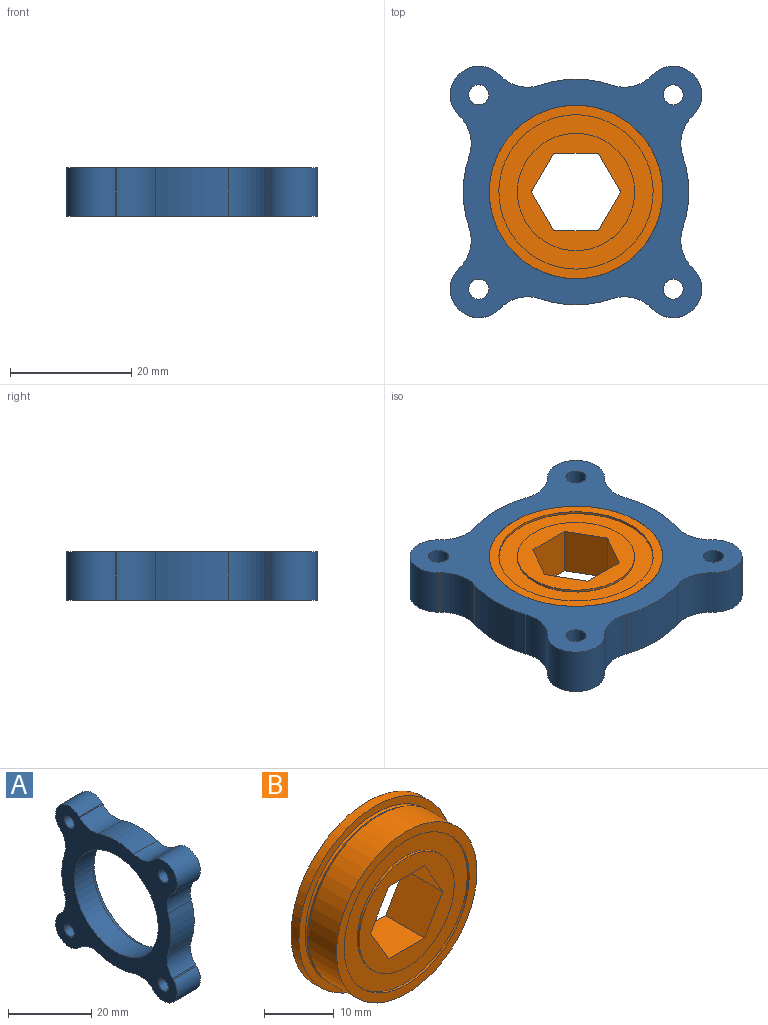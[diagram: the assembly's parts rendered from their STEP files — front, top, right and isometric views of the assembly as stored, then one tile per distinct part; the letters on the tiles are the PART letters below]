
ASSEMBLY  parts=2 mates=1
PART A: 33 faces, bbox 7.9x41.4x41.4 mm
  f0: cylinder r=4.7mm len=8.03mm, axis (1,0,0), area 117.3mm2, adj f1,f15,f17,f19
  f1: plane 7.94x0.22mm, normal (0,0.71,0.71), area 2.4mm2, adj f0,f17,f19,f25
  f2: cylinder r=18.56mm len=11.87mm, axis (1,0,0), area 95.9mm2, adj f17,f19,f25,f26
  f3: plane 7.94x0.22mm, normal (0,-0.71,0.71), area 2.4mm2, adj f4,f17,f19,f26
  f4: cylinder r=4.7mm len=8.03mm, axis (1,0,0), area 117.3mm2, adj f3,f5,f17,f19
  f5: plane 7.94x0.22mm, normal (0,0.71,-0.71), area 2.4mm2, adj f4,f17,f19,f27
  f6: cylinder r=18.56mm len=11.87mm, axis (1,0,0), area 95.9mm2, adj f17,f19,f27,f28
  f7: plane 7.94x0.22mm, normal (0,0.71,0.71), area 2.4mm2, adj f8,f17,f19,f28
  f8: cylinder r=4.7mm len=8.03mm, axis (1,0,0), area 117.3mm2, adj f7,f9,f17,f19
  f9: plane 7.94x0.22mm, normal (0,-0.71,-0.71), area 2.4mm2, adj f8,f17,f19,f29
  f10: cylinder r=18.56mm len=11.87mm, axis (1,0,0), area 95.9mm2, adj f17,f19,f29,f30
  f11: plane 7.94x0.22mm, normal (0,0.71,-0.71), area 2.4mm2, adj f12,f17,f19,f30
  f12: cylinder r=4.7mm len=8.03mm, axis (1,0,0), area 117.3mm2, adj f11,f13,f17,f19
  f13: plane 7.94x0.22mm, normal (0,-0.71,0.71), area 2.4mm2, adj f12,f17,f19,f31
  f14: cylinder r=18.56mm len=11.87mm, axis (1,0,0), area 95.9mm2, adj f17,f19,f31,f32
  f15: plane 7.94x0.22mm, normal (0,-0.71,-0.71), area 2.4mm2, adj f0,f17,f19,f32
  f16: cylinder r=15.56mm len=31.12mm, axis (1,0,0), area 155.2mm2, adj f17,f18
  f17: plane 41.41x41.41mm, normal (1,0,0), area 612.1mm2, adj f0,f1,f2,f3,f4,f5,f6,f7
  f18: plane 31.12x31.12mm, normal (1,0,0), area 120.2mm2, adj f16,f20
  f19: plane 41.41x41.41mm, normal (-1,0,0), area 732.3mm2, adj f0,f1,f2,f3,f4,f5,f6,f7
  f20: cylinder r=14.27mm len=28.55mm, axis (1,0,0), area 569.5mm2, adj f18,f19
  f21: cylinder r=1.65mm len=7.94mm, axis (-1,0,0), area 82.3mm2, adj f17,f19
  f22: cylinder r=1.65mm len=7.94mm, axis (-1,0,0), area 82.3mm2, adj f17,f19
  f23: cylinder r=1.65mm len=7.94mm, axis (-1,0,0), area 82.3mm2, adj f17,f19
  f24: cylinder r=1.65mm len=7.94mm, axis (-1,0,0), area 82.3mm2, adj f17,f19
  f25: cylinder r=6.35mm len=7.94mm, axis (1,0,0), area 56mm2, adj f1,f2,f17,f19
  f26: cylinder r=6.35mm len=7.94mm, axis (1,0,0), area 56mm2, adj f2,f3,f17,f19
  f27: cylinder r=6.35mm len=7.94mm, axis (1,0,0), area 56mm2, adj f5,f6,f17,f19
  f28: cylinder r=6.35mm len=7.94mm, axis (1,0,0), area 56mm2, adj f6,f7,f17,f19
  f29: cylinder r=6.35mm len=7.94mm, axis (1,0,0), area 56mm2, adj f9,f10,f17,f19
  f30: cylinder r=6.35mm len=7.94mm, axis (1,0,0), area 56mm2, adj f10,f11,f17,f19
  f31: cylinder r=6.35mm len=7.94mm, axis (1,0,0), area 56mm2, adj f13,f14,f17,f19
  f32: cylinder r=6.35mm len=7.94mm, axis (1,0,0), area 56mm2, adj f14,f15,f17,f19
PART B: 21 faces, bbox 31.1x7.9x31.1 mm
  f0: torus R=14.27mm, axis (0,1,0), area 46.4mm2, adj f4,f10
  f1: cylinder r=9.65mm len=19.3mm, axis (0,1,0), area 23.1mm2, adj f12,f13
  f2: cylinder r=12.7mm len=25.4mm, axis (0,1,0), area 30.4mm2, adj f11,f12
  f3: cylinder r=14.27mm len=28.55mm, axis (0,1,0), area 502.3mm2, adj f4,f11
  f4: cone r=14.06mm half-angle=30deg, axis (0,-1,0), area 38.5mm2, adj f0,f3
  f5: cylinder r=15.56mm len=31.12mm, axis (0,1,0), area 155.2mm2, adj f9,f10
  f6: cylinder r=12.7mm len=25.4mm, axis (0,1,0), area 30.4mm2, adj f8,f9
  f7: cylinder r=9.65mm len=19.3mm, axis (0,1,0), area 23.1mm2, adj f8,f14
  f8: plane 25.4x25.4mm, normal (0,1,0), area 214mm2, adj f6,f7
  f9: plane 31.12x31.12mm, normal (0,1,0), area 253.7mm2, adj f5,f6
  f10: plane 31.12x31.12mm, normal (0,-1,0), area 120.2mm2, adj f0,f5
  f11: plane 28.55x28.55mm, normal (0,-1,0), area 133.5mm2, adj f2,f3
  f12: plane 25.4x25.4mm, normal (0,-1,0), area 214mm2, adj f1,f2
  f13: plane 19.3x19.3mm, normal (0,-1,0), area 152.6mm2, adj f1,f15,f16,f17,f18,f19,f20
  f14: plane 19.3x19.3mm, normal (0,1,0), area 152.6mm2, adj f7,f15,f16,f17,f18,f19,f20
  f15: plane 7.94x6.36mm, normal (-0.87,0,0.5), area 58.3mm2, adj f13,f14,f16,f20
  f16: plane 7.94x6.36mm, normal (-0.87,0,-0.5), area 58.3mm2, adj f13,f14,f15,f17
  f17: plane 7.94x7.34mm, normal (0,0,-1), area 58.3mm2, adj f13,f14,f16,f18
  f18: plane 7.94x6.36mm, normal (0.87,0,-0.5), area 58.3mm2, adj f13,f14,f17,f19
  f19: plane 7.94x6.36mm, normal (0.87,0,0.5), area 58.3mm2, adj f13,f14,f18,f20
  f20: plane 7.94x7.34mm, normal (0,0,1), area 58.3mm2, adj f13,f14,f15,f19
PLACE A rot(axis=(0,1,0),90deg) t=(47.55,-8.63,-29.57)mm
PLACE B rot(axis=(0,-0.71,0.71),180deg) t=(-29.78,-1.91,-2.79)mm
MATE fastened A.f20 <-> B.f0  axis (0,0,-1) through (-29.78,-1.91,-9.14)mm
